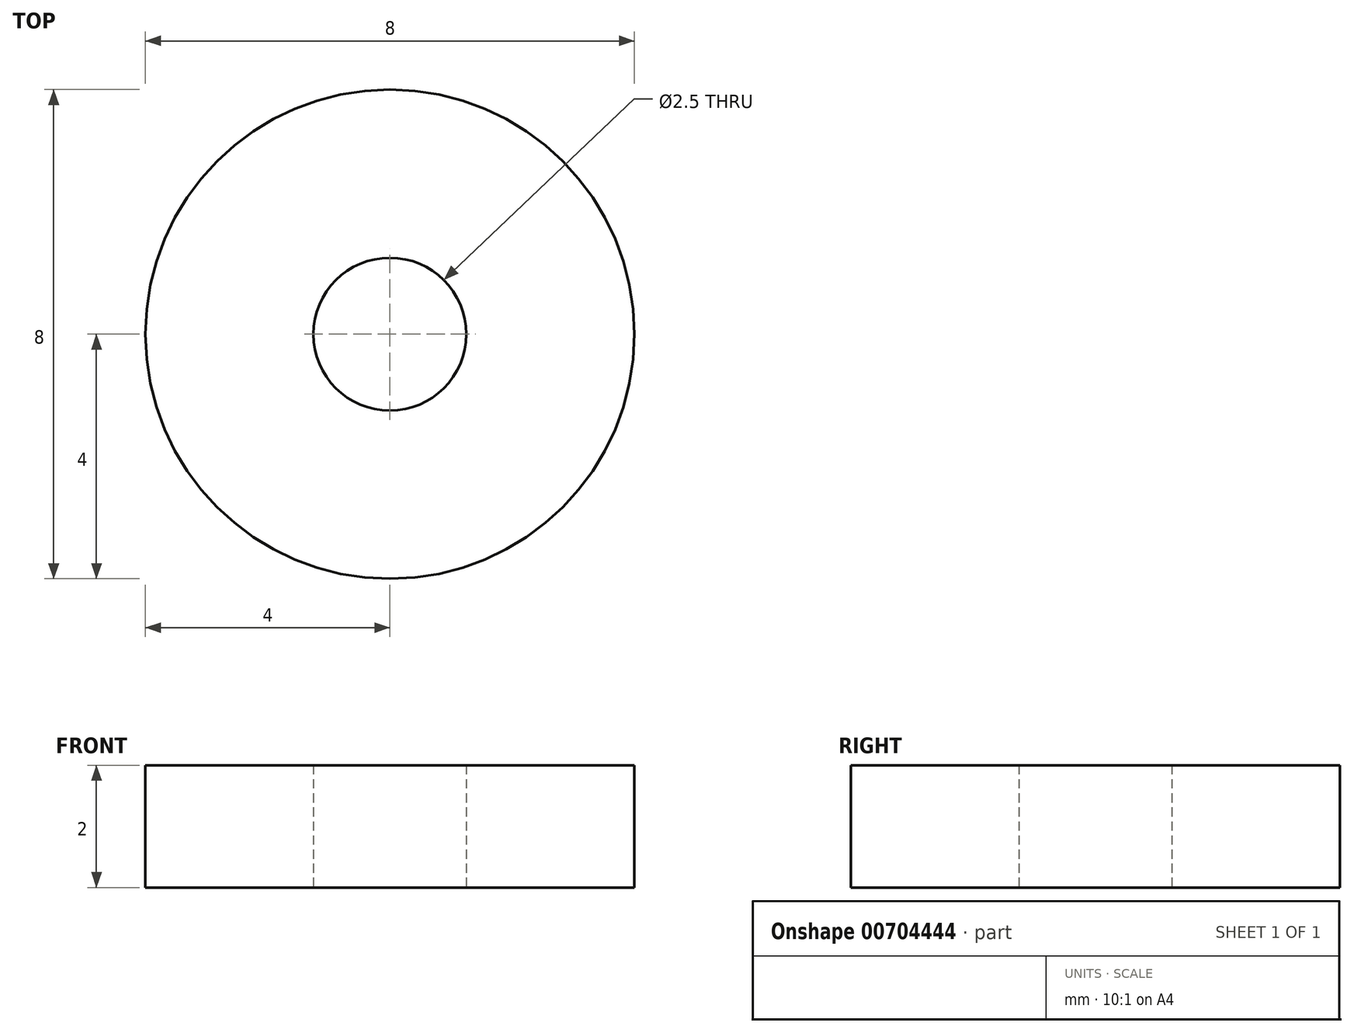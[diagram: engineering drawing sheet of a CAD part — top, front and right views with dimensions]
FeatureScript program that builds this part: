
annotation { "Feature Type Name" : "Feature", "Feature Type Description" : "" }
export const myFeature = defineFeature(function(context is Context, id is Id, definition is map)
    precondition{}
    {
        {
            var Q0;
            Q0=qCreatedBy(makeId("Top.planeOp"),FACE);
            var sketch = newSketch(context, id + "F0", { "sketchPlane" : qUnion([Q0])});
            skCircle(sketch, "E0", {"center": v(0, 0) * mm, "radius": 4 * mm});
            skCircle(sketch, "E1", {"center": v(0, 0) * mm, "radius": 1.25 * mm});
            skSolve(sketch);
        }
        {
            var Q0;
            Q0=makeQuery(id+"F0.imprint","IMPRINT",FACE,{"disambiguationData":[TD([[makeQuery(id+"F0.imprint","IMPRINT",EDGE,{"derivedFrom":sQuery(id+"F0.wireOp",EDGE,"E0")}),1.0]])]});
            extrude(context, id + "F1", {"entities" : qUnion([Q0]), "depth" : 2 * mm, "offsetDistance" : 25 * mm});
        }
    });
